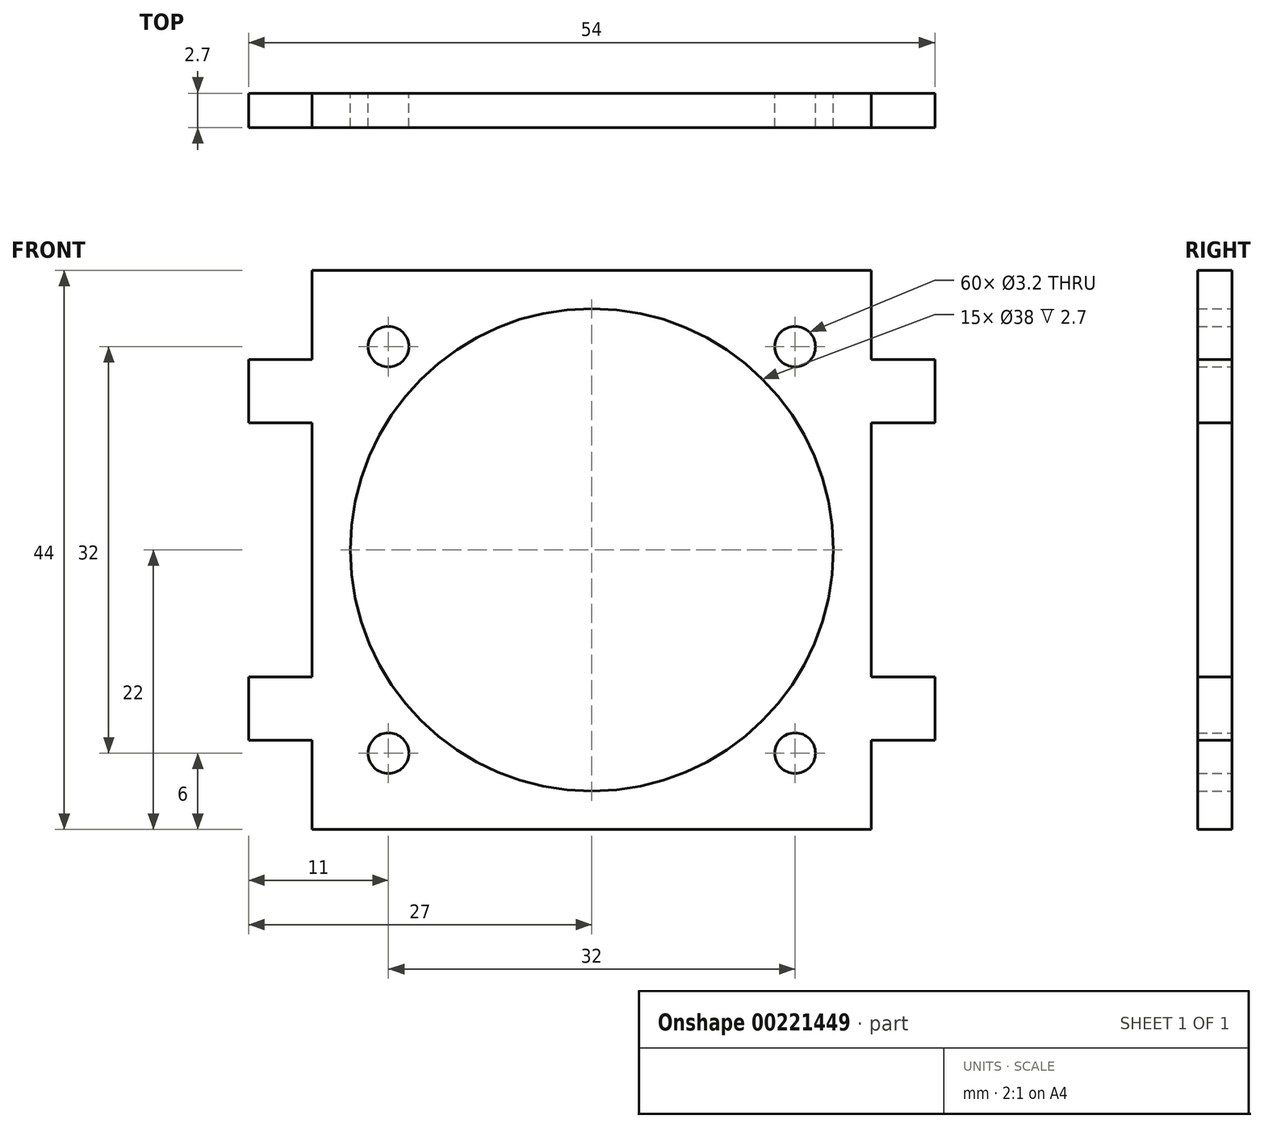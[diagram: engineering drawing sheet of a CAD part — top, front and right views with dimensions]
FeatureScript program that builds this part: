
annotation { "Feature Type Name" : "Feature", "Feature Type Description" : "" }
export const myFeature = defineFeature(function(context is Context, id is Id, definition is map)
    precondition{}
    {
        {
            var Q0;
            Q0=qCreatedBy(makeId("Front.planeOp"),FACE);
            var sketch = newSketch(context, id + "F0", { "sketchPlane" : qUnion([Q0])});
            skLineSegment(sketch, "E0.bottom", {"start": v(22, 22) * mm, "end": v(-22, 22) * mm});
            skLineSegment(sketch, "E0.top", {"start": v(22, -22) * mm, "end": v(-22, -22) * mm});
            skLineSegment(sketch, "E0.left", {"start": v(22, 22) * mm, "end": v(22, -22) * mm});
            skLineSegment(sketch, "E0.right", {"start": v(-22, 22) * mm, "end": v(-22, -22) * mm});
            skPoint(sketch, "E0.middle", {"position": v(0, 0) * mm});
            skLineSegment(sketch, "E1.bottom", {"start": v(16, 16) * mm, "end": v(-16, 16) * mm, "construction": true});
            skLineSegment(sketch, "E1.top", {"start": v(16, -16) * mm, "end": v(-16, -16) * mm, "construction": true});
            skLineSegment(sketch, "E1.left", {"start": v(16, 16) * mm, "end": v(16, -16) * mm, "construction": true});
            skLineSegment(sketch, "E1.right", {"start": v(-16, 16) * mm, "end": v(-16, -16) * mm, "construction": true});
            skCircle(sketch, "E2", {"center": v(-16, 16) * mm, "radius": 1.6 * mm});
            skCircle(sketch, "E3", {"center": v(16, 16) * mm, "radius": 1.6 * mm});
            skCircle(sketch, "E4", {"center": v(-16, -16) * mm, "radius": 1.6 * mm});
            skCircle(sketch, "E5", {"center": v(16, -16) * mm, "radius": 1.6 * mm});
            skCircle(sketch, "E6", {"center": v(0, 0) * mm, "radius": 19 * mm});
            skLineSegment(sketch, "E7", {"start": v(-22, 15) * mm, "end": v(-27, 15) * mm});
            skLineSegment(sketch, "E8", {"start": v(-27, 15) * mm, "end": v(-27, 10) * mm});
            skLineSegment(sketch, "E9", {"start": v(-27, 10) * mm, "end": v(-22, 10) * mm});
            skLineSegment(sketch, "E10", {"start": v(-22, -10) * mm, "end": v(-27, -10) * mm});
            skLineSegment(sketch, "E11", {"start": v(-27, -10) * mm, "end": v(-27, -15) * mm});
            skLineSegment(sketch, "E12", {"start": v(-27, -15) * mm, "end": v(-22, -15) * mm});
            skLineSegment(sketch, "E13", {"start": v(0, 22) * mm, "end": v(0, -22) * mm, "construction": true});
            skLineSegment(sketch, "E14.MirrorCS", {"start": v(27, 15) * mm, "end": v(27, 10) * mm});
            skLineSegment(sketch, "E15.MirrorCS", {"start": v(22, 15) * mm, "end": v(27, 15) * mm});
            skLineSegment(sketch, "E16.MirrorCS", {"start": v(27, 10) * mm, "end": v(22, 10) * mm});
            skLineSegment(sketch, "E17.MirrorCS", {"start": v(22, -10) * mm, "end": v(27, -10) * mm});
            skLineSegment(sketch, "E18.MirrorCS", {"start": v(27, -10) * mm, "end": v(27, -15) * mm});
            skLineSegment(sketch, "E19.MirrorCS", {"start": v(27, -15) * mm, "end": v(22, -15) * mm});
            skSolve(sketch);
        }
        {
            var Q0;
            Q0 = qSketchRegion(id + "F0", true);
            extrude(context, id + "F1", {"entities" : qUnion([Q0]), "depth" : 2.7 * mm});
        }
    });
